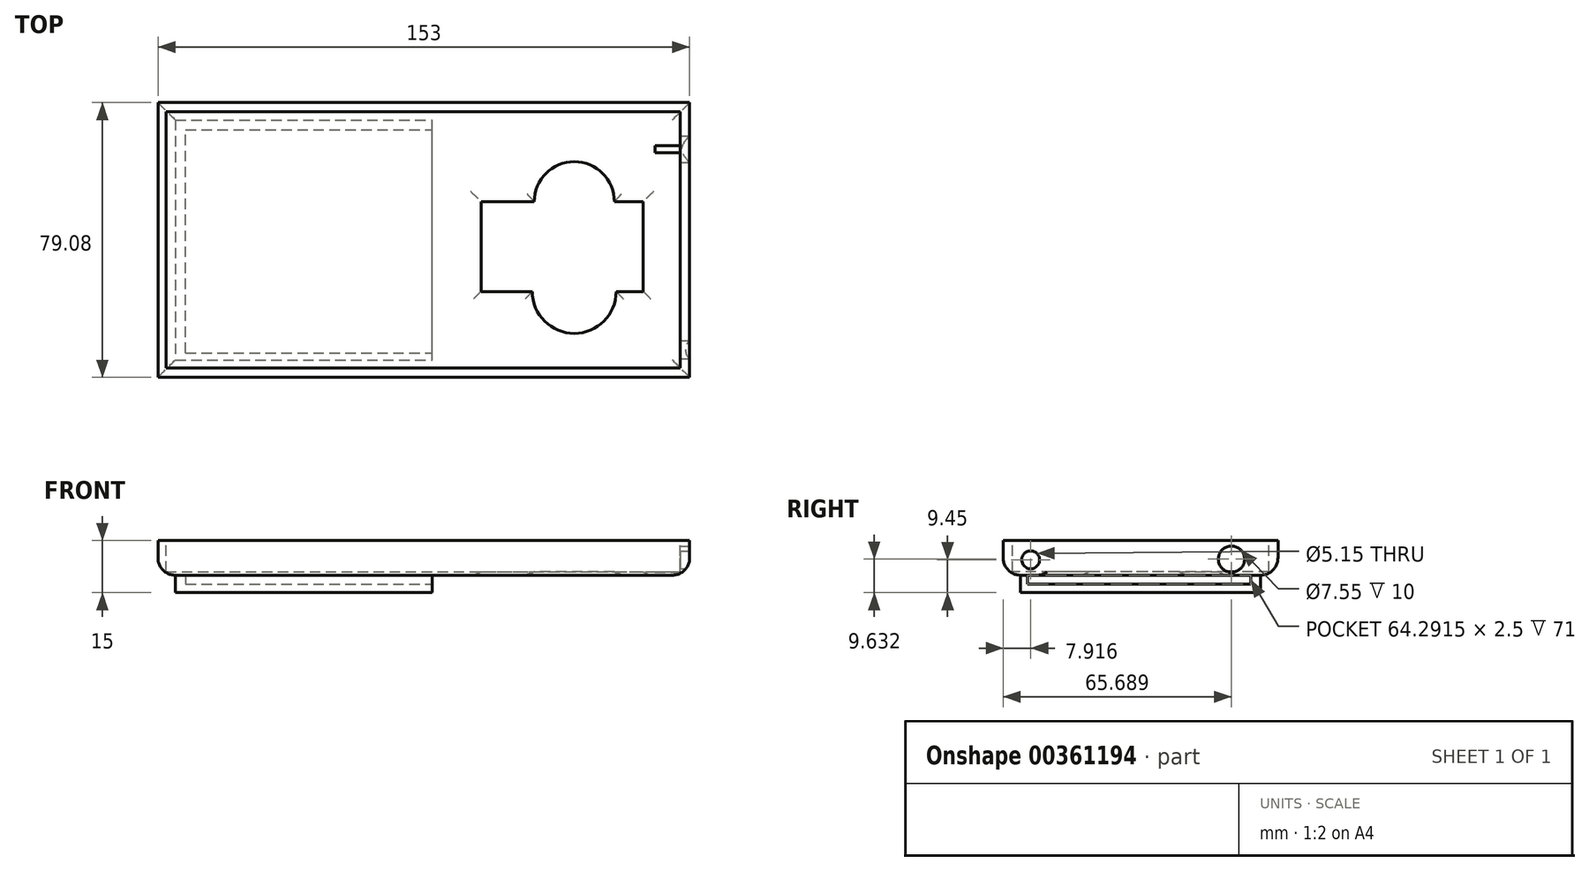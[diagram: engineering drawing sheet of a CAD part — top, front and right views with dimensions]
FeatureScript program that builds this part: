
annotation { "Feature Type Name" : "Feature", "Feature Type Description" : "" }
export const myFeature = defineFeature(function(context is Context, id is Id, definition is map)
    precondition{}
    {
        {
            var Q0;
            Q0=qCreatedBy(makeId("Top.planeOp"),FACE);
            var sketch = newSketch(context, id + "F0", { "sketchPlane" : qUnion([Q0])});
            skLineSegment(sketch, "E0.bottom", {"start": v(-78.92, 54.38) * mm, "end": v(74.08, 54.38) * mm});
            skLineSegment(sketch, "E0.top", {"start": v(-78.92, -24.7) * mm, "end": v(74.08, -24.7) * mm});
            skLineSegment(sketch, "E0.left", {"start": v(-78.92, 54.38) * mm, "end": v(-78.92, -24.7) * mm});
            skLineSegment(sketch, "E0.right", {"start": v(74.08, 54.38) * mm, "end": v(74.08, -24.7) * mm});
            skSolve(sketch);
        }
        {
            var Q0;
            Q0 = qSketchRegion(id + "F0", true);
            var Q1;
            Q1 = qSketchRegion(id + "F2", true);
            extrude(context, id + "F1", {"entities" : qUnion([Q0, Q1]), "depth" : 10 * mm});
        }
        {
            var Q0;
            Q0=makeQuery(id+"F1.opExtrude","SWEPT_FACE",FACE,{"disambiguationData":[OSD([sQuery(id+"F0.wireOp",EDGE,"E0.right")])]});
            var sketch = newSketch(context, id + "F2", { "sketchPlane" : qUnion([Q0])});
            skCircle(sketch, "E1", {"center": v(-16.78, 4.45) * mm, "radius": 2.58 * mm});
            skSolve(sketch);
        }
        {
            var Q0;
            Q0=makeQuery(id+"F1.opExtrude","CAP_FACE",FACE,{"disambiguationData":[OSD([sQuery(id+"F0.wireOp",EDGE,"E0.bottom"),sQuery(id+"F0.wireOp",EDGE,"E0.top"),sQuery(id+"F0.wireOp",EDGE,"E0.left"),sQuery(id+"F0.wireOp",EDGE,"E0.right")])],"isStart":false});
            var sketch = newSketch(context, id + "F3", { "sketchPlane" : qUnion([Q0])});
            skLineSegment(sketch, "E2.bottom", {"start": v(-76.64, 51.8) * mm, "end": v(71.32, 51.8) * mm});
            skLineSegment(sketch, "E2.top", {"start": v(-76.64, -22.04) * mm, "end": v(71.32, -22.04) * mm});
            skLineSegment(sketch, "E2.left", {"start": v(-76.64, 51.8) * mm, "end": v(-76.64, -22.04) * mm});
            skLineSegment(sketch, "E2.right", {"start": v(71.32, 51.8) * mm, "end": v(71.32, -22.04) * mm});
            skSolve(sketch);
        }
        {
            var Q0;
            Q0=makeQuery(id+"F3.imprint","IMPRINT",FACE,{"disambiguationData":[TD([[makeQuery(id+"F3.imprint","IMPRINT",EDGE,{"derivedFrom":sQuery(id+"F3.wireOp",EDGE,"E2.bottom")}),-1.0]])]});
            extrude(context, id + "F4", {"entities" : qUnion([Q0]), "operationType" : NewBodyOperationType.REMOVE, "oppositeDirection" : true, "depth" : 9 * mm});
        }
        {
            var Q0;
            Q0=makeQuery(id+"F2.imprint","IMPRINT",FACE,{"disambiguationData":[TD([[makeQuery(id+"F2.imprint","IMPRINT",EDGE,{"derivedFrom":sQuery(id+"F2.wireOp",EDGE,"E1")}),1.0]])]});
            extrude(context, id + "F5", {"entities" : qUnion([Q0]), "operationType" : NewBodyOperationType.REMOVE, "oppositeDirection" : true, "depth" : 25 * mm});
        }
        {
            var Q0;
            Q0=makeQuery(id+"F1.opExtrude","SWEPT_FACE",FACE,{"disambiguationData":[OSD([sQuery(id+"F0.wireOp",EDGE,"E0.right")])]});
            var sketch = newSketch(context, id + "F6", { "sketchPlane" : qUnion([Q0])});
            skCircle(sketch, "E3", {"center": v(40.99, 4.63) * mm, "radius": 3.78 * mm});
            skSolve(sketch);
        }
        {
            var Q0;
            Q0 = qSketchRegion(id + "F6", true);
            extrude(context, id + "F7", {"entities" : qUnion([Q0]), "operationType" : NewBodyOperationType.REMOVE, "oppositeDirection" : true, "depth" : 10 * mm});
        }
        {
            var Q0;
            Q0=makeQuery(id+"F1.opExtrude","CAP_FACE",FACE,{"disambiguationData":[OSD([sQuery(id+"F0.wireOp",EDGE,"E0.bottom"),sQuery(id+"F0.wireOp",EDGE,"E0.top"),sQuery(id+"F0.wireOp",EDGE,"E0.left"),sQuery(id+"F0.wireOp",EDGE,"E0.right")])],"isStart":true});
            var sketch = newSketch(context, id + "F8", { "sketchPlane" : qUnion([Q0])});
            skLineSegment(sketch, "E4", {"start": v(60.75, -25.85) * mm, "end": v(60.75, 0) * mm});
            skLineSegment(sketch, "E5", {"start": v(60.75, 0) * mm, "end": v(45.54, 0) * mm});
            skLineSegment(sketch, "E6", {"start": v(45.54, 0) * mm, "end": v(14.03, 0) * mm});
            skPoint(sketch, "E7.end.orphan", {"position": v(14.03, -23.92) * mm});
            skPoint(sketch, "E8.start.orphan", {"position": v(14.03, -25.85) * mm});
            skLineSegment(sketch, "E9", {"start": v(60.75, -25.85) * mm, "end": v(14.03, -25.85) * mm});
            skPoint(sketch, "E10.start.orphan", {"position": v(11.82, -25.85) * mm});
            skLineSegment(sketch, "E11", {"start": v(14.03, 0) * mm, "end": v(14.03, -25.85) * mm});
            skSolve(sketch);
        }
        {
            var Q0;
            Q0 = qSketchRegion(id + "F8", true);
            extrude(context, id + "F9", {"entities" : qUnion([Q0]), "operationType" : NewBodyOperationType.REMOVE, "oppositeDirection" : true, "depth" : 25 * mm});
        }
        {
            var Q0;
            Q0=makeQuery(id+"F1.opExtrude","CAP_FACE",FACE,{"disambiguationData":[OSD([sQuery(id+"F0.wireOp",EDGE,"E0.bottom"),sQuery(id+"F0.wireOp",EDGE,"E0.top"),sQuery(id+"F0.wireOp",EDGE,"E0.left"),sQuery(id+"F0.wireOp",EDGE,"E0.right")])],"isStart":true});
            var sketch = newSketch(context, id + "F10", { "sketchPlane" : qUnion([Q0])});
            skCircle(sketch, "E12", {"center": v(40.88, 0) * mm, "radius": 12.07 * mm});
            skCircle(sketch, "E13", {"center": v(40.88, -25.85) * mm, "radius": 11.52 * mm});
            skSolve(sketch);
        }
        {
            var Q0;
            Q0 = qSketchRegion(id + "F10", true);
            extrude(context, id + "F11", {"entities" : qUnion([Q0]), "operationType" : NewBodyOperationType.REMOVE, "oppositeDirection" : true, "depth" : 25 * mm});
        }
        {
            var Q0;
            Q0=makeQuery(id+"F1.opExtrude","CAP_EDGE",EDGE,{"disambiguationData":[OSD([sQuery(id+"F0.wireOp",EDGE,"E0.right")])],"isStart":true});
            var Q1;
            Q1=makeQuery(id+"F1.opExtrude","CAP_FACE",FACE,{"disambiguationData":[OSD([sQuery(id+"F0.wireOp",EDGE,"E0.bottom"),sQuery(id+"F0.wireOp",EDGE,"E0.top"),sQuery(id+"F0.wireOp",EDGE,"E0.left"),sQuery(id+"F0.wireOp",EDGE,"E0.right")])],"isStart":true});
            fillet(context, id + "F12", {"entities" : qUnion([Q0, Q1]), "radius" : 5 * mm, "tangentPropagation" : true, "allowEdgeOverflow" : false});
        }
        {
            var Q0;
            Q0=makeQuery(id+"F1.opExtrude","CAP_FACE",FACE,{"disambiguationData":[OSD([sQuery(id+"F0.wireOp",EDGE,"E0.bottom"),sQuery(id+"F0.wireOp",EDGE,"E0.top"),sQuery(id+"F0.wireOp",EDGE,"E0.left"),sQuery(id+"F0.wireOp",EDGE,"E0.right")])],"isStart":true});
            var sketch = newSketch(context, id + "F13", { "sketchPlane" : qUnion([Q0])});
            skPoint(sketch, "E14.firstSnap0", {"position": v(-2.42, 19.7) * mm});
            skLineSegment(sketch, "E14.bottom", {"start": v(0, 19.7) * mm, "end": v(-73.92, 19.7) * mm});
            skLineSegment(sketch, "E14.top", {"start": v(0, -49.38) * mm, "end": v(-73.92, -49.38) * mm});
            skLineSegment(sketch, "E14.left", {"start": v(0, 19.7) * mm, "end": v(0, -49.38) * mm});
            skLineSegment(sketch, "E14.right", {"start": v(-73.92, 19.7) * mm, "end": v(-73.92, -49.38) * mm});
            skSolve(sketch);
        }
        {
            var Q0;
            Q0=makeQuery(id+"F13.imprint","IMPRINT",FACE,{"disambiguationData":[TD([[makeQuery(id+"F13.imprint","IMPRINT",EDGE,{"derivedFrom":sQuery(id+"F13.wireOp",EDGE,"E14.bottom")}),1.0]])]});
            extrude(context, id + "F14", {"entities" : qUnion([Q0]), "operationType" : NewBodyOperationType.ADD, "depth" : 5 * mm});
        }
        {
            var Q0;
            Q0=makeQuery(id+"F14.opExtrude","SWEPT_FACE",FACE,{"disambiguationData":[OSD([sQuery(id+"F13.wireOp",EDGE,"E14.left")])]});
            var sketch = newSketch(context, id + "F15", { "sketchPlane" : qUnion([Q0])});
            skPoint(sketch, "E15.oppositeSnap0", {"position": v(49.38, -2.5) * mm});
            skLineSegment(sketch, "E15.bottom", {"start": v(-17.69, 0) * mm, "end": v(46.6, 0) * mm});
            skLineSegment(sketch, "E15.top", {"start": v(-17.69, -2.5) * mm, "end": v(46.6, -2.5) * mm});
            skLineSegment(sketch, "E15.left", {"start": v(-17.69, 0) * mm, "end": v(-17.69, -2.5) * mm});
            skLineSegment(sketch, "E15.right", {"start": v(46.6, 0) * mm, "end": v(46.6, -2.5) * mm});
            skSolve(sketch);
        }
        {
            var Q0;
            Q0 = qSketchRegion(id + "F15", true);
            extrude(context, id + "F16", {"entities" : qUnion([Q0]), "operationType" : NewBodyOperationType.REMOVE, "oppositeDirection" : true, "depth" : 71 * mm});
        }
    });
